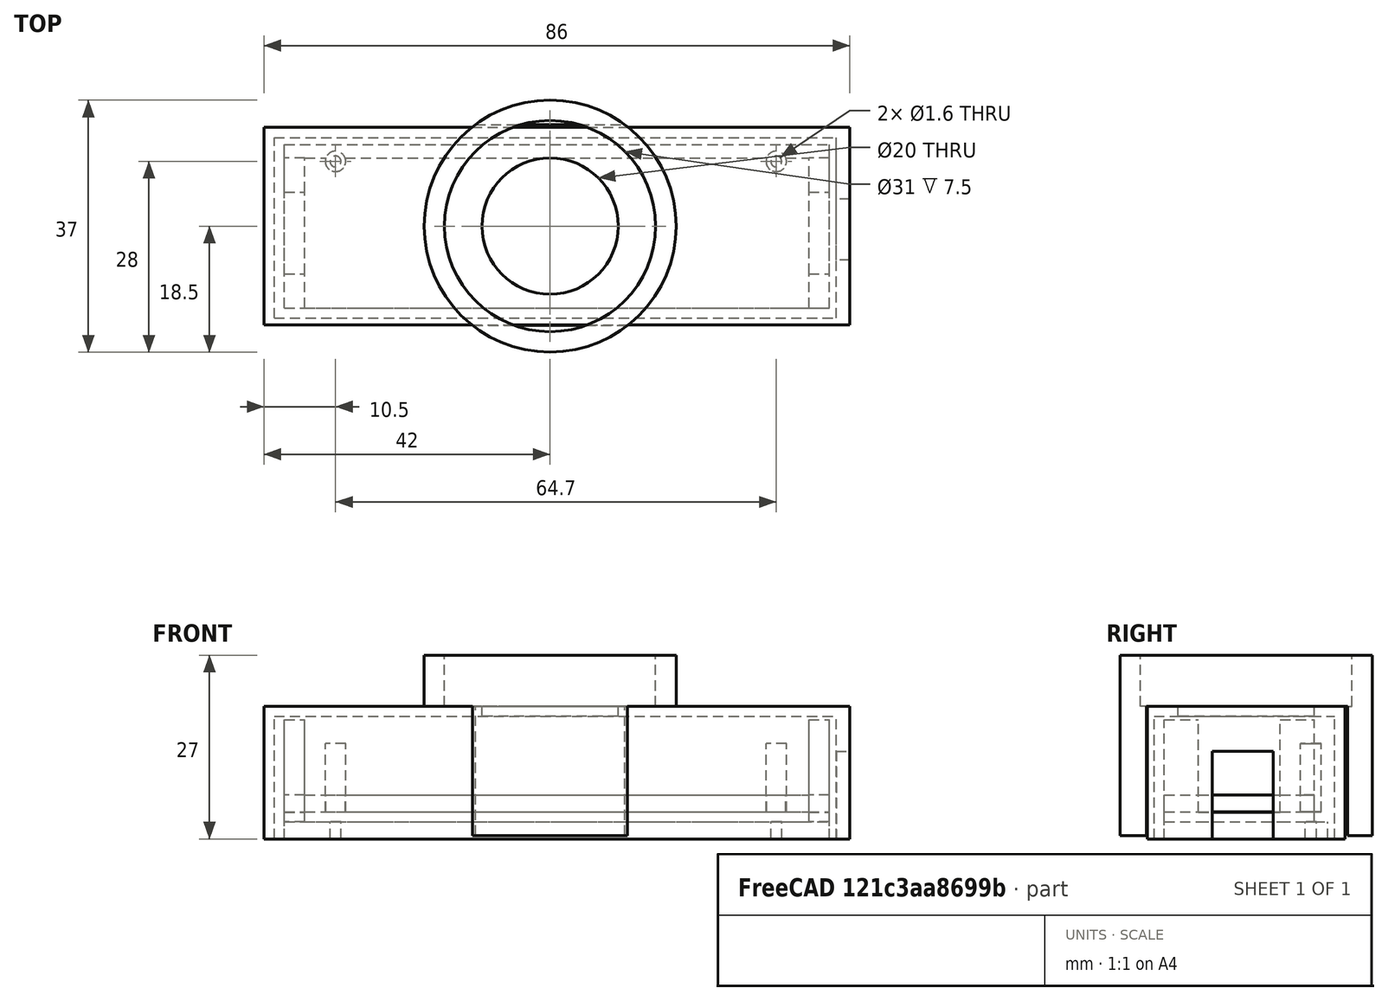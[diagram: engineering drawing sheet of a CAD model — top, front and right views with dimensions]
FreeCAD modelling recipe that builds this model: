
FCSTD DOCUMENT  (FreeCAD 0.18.4R)
Label: c920-telescope-adapter
License: All rights reserved
LicenseURL: http://en.wikipedia.org/wiki/All_rights_reserved
objects: Part::Box×19, Part::Cylinder×11, Part::MultiFuse×7, Part::Cut×7, Drawing::FeatureViewPart×1, Drawing::FeaturePage×1
note: 44 computed .brp shape members not serialized (recipe doc carries the construction recipe); baked Part::Feature solids carry a one-line shape summary decoded from their .brp

FEATURE [Part::Box] Box  label="pre-pci-board"
  AttacherType = Attacher::AttachEngine3D
  Height = 2.5
  Length = 80
  Width = 22
FEATURE [Part::Box] Box001  label="Cube"
  AttacherType = Attacher::AttachEngine3D
  Height = 10
  Length = 3
  Width = 5
FEATURE [Part::Box] Box002  label="Cube001"
  AttacherType = Attacher::AttachEngine3D
  Height = 10
  Length = 3
  Placement = pos=(77,0,0) rot=(0,0,1;0rad)
  Width = 5
FEATURE [Part::Box] Box003  label="Cube002"
  AttacherType = Attacher::AttachEngine3D
  Height = 10
  Length = 3
  Placement = pos=(77,17,0) rot=(0,0,1;0rad)
  Width = 5
FEATURE [Part::Box] Box004  label="Cube003"
  AttacherType = Attacher::AttachEngine3D
  Height = 10
  Length = 3
  Placement = pos=(0,17,0) rot=(0,0,1;0rad)
  Width = 5
FEATURE [Part::Cylinder] Cylinder
  Angle = 360
  AttacherType = Attacher::AttachEngine3D
  Height = 10
  Placement = pos=(7.5,21.5,0) rot=(0,0,1;0rad)
  Radius = 1.5
FEATURE [Part::Cylinder] Cylinder001
  Angle = 360
  AttacherType = Attacher::AttachEngine3D
  Height = 10
  Placement = pos=(72.2,21.5,0) rot=(0,0,1;0rad)
  Radius = 1.5
FEATURE [Part::MultiFuse] Fusion
  Shapes = -> [Cylinder001,Cylinder,Box004,Box003,Box002,Box001]
FEATURE [Part::Cut] Cut  label="simple-pci-board"
  Base = -> Box
  Tool = -> Fusion
FEATURE [Drawing::FeatureViewPart] Ortho  label="Ortho_0_0"
  Direction = (0,0,1)
  HiddenWidth = 0.15
  LineWidth = 0.35
  Rotation = 0
  ShowHiddenLines = false
  ShowSmoothLines = false
  Source = -> Cut
  Tolerance = 0.05
  ViewResult = <g id="Ortho_0_0"\n   transform="rotate(0,108.5,92.5) translate(108.5,92.5) scale(1,1)"\n  >\n<g   fill="none"\n   stroke="rgb(0, 0, 0)"\n   stroke-linecap="butt"\n   stroke-linejoin="miter"\n   stroke-width="0.350000"\n   transform="scale(1,-1)"\n  >\n<path id= "1" d=" M 0 5 L 0 17 " />\n<path id= "2" d=" M 3 5 L 0 5 " />\n<path id= "3" d=" M 3 17 L 0 17 " />\n<path id= "4" d=" M 3 17 L 3 22 " />\n<path id= "5" d=" M 3 22 L 6.08579 22 " />\n<path d="M6.08579 22 A1.5 1.5 0 1 1 9 21.5" /><path d="M9 21.5 A1.5 1.5 0 0 1 8.91421 22" /><path id= "8" d=" M 8.91421 22 L 70.7858 22 " />\n<path d="M70.7858 22 A1.5 1.5 0 1 1 73.7 21.5" /><path d="M73.7 21.5 A1.5 1.5 0 0 1 73.6142 22" /><path id= "11" d=" M 73.6142 22 L 77 22 " />\n<path id= "12" d=" M 77 17 L 77 22 " />\n<path id= "13" d=" M 80 17 L 77 17 " />\n<path id= "14" d=" M 80 5 L 80 17 " />\n<path id= "15" d=" M 80 5 L 77 5 " />\n<path id= "16" d=" M 77 0 L 77 5 " />\n<path id= "17" d=" M 3 0 L 77 0 " />\n<path id= "18" d=" M 3 0 L 3 5 " />\n</g>\n</g>
  Visible = true
  X = 108.5
  Y = 92.5
FEATURE [Drawing::FeaturePage] Page
  EditableTexts = Jose Damico | 2020-May-18 | 1x1 | -- | Basic Pci Board | Simple View | 1 | 1
  Group = -> [Ortho]
  Template = <path>
FEATURE [Part::Cylinder] Cylinder002
  Angle = 360
  AttacherType = Attacher::AttachEngine3D
  Height = 10
  Placement = pos=(72.2,21.5,0) rot=(0,0,1;0rad)
  Radius = 1.5
FEATURE [Part::Cylinder] Cylinder003
  Angle = 360
  AttacherType = Attacher::AttachEngine3D
  Height = 10
  Placement = pos=(7.5,21.5,0) rot=(0,0,1;0rad)
  Radius = 1.5
FEATURE [Part::Box] Box005  label="Cube004"
  AttacherType = Attacher::AttachEngine3D
  Height = 15.5
  Length = 3
  Placement = pos=(0,17,-2) rot=(0,0,1;0rad)
  Width = 5
FEATURE [Part::Box] Box006  label="Cube005"
  AttacherType = Attacher::AttachEngine3D
  Height = 15.5
  Length = 3
  Placement = pos=(77,17,-2) rot=(0,0,1;0rad)
  Width = 5
FEATURE [Part::Box] Box007  label="Cube006"
  AttacherType = Attacher::AttachEngine3D
  Height = 15.5
  Length = 3
  Placement = pos=(77,0,-2) rot=(0,0,1;0rad)
  Width = 5
FEATURE [Part::Box] Box008  label="Cube007"
  AttacherType = Attacher::AttachEngine3D
  Height = 15.5
  Length = 3
  Placement = pos=(0,0,-2) rot=(0,0,1;0rad)
  Width = 5
FEATURE [Part::Box] Box009  label="pre-pci-board001"
  AttacherType = Attacher::AttachEngine3D
  Height = 2.5
  Length = 80
  Placement = pos=(0,0,-4) rot=(0,0,1;0rad)
  Width = 24
FEATURE [Part::Box] Box010  label="Cube008"
  AttacherType = Attacher::AttachEngine3D
  Height = 2
  Length = 3
  Placement = pos=(0,5,-2.1) rot=(0,0,1;0rad)
  Width = 12
FEATURE [Part::Box] Box011  label="Cube009"
  AttacherType = Attacher::AttachEngine3D
  Height = 2
  Length = 3
  Placement = pos=(77,5,-2.1) rot=(0,0,1;0rad)
  Width = 12
FEATURE [Part::Box] Box012  label="pre-pci-board002"
  AttacherType = Attacher::AttachEngine3D
  Height = 19.5
  Length = 86
  Placement = pos=(-3,-2.5,-4) rot=(0,0,1;0rad)
  Width = 29
FEATURE [Part::MultiFuse] Fusion001
  Shapes = -> [Box011,Box010,Box008,Box007,Box006,Box005]
FEATURE [Part::Box] Box013  label="pre-pci-board003"
  AttacherType = Attacher::AttachEngine3D
  Height = 18
  Length = 82.5
  Placement = pos=(-1.5,-1.5,-4) rot=(0,0,1;0rad)
  Width = 26.5
FEATURE [Part::Cylinder] Cylinder004
  Angle = 360
  AttacherType = Attacher::AttachEngine3D
  Height = 24
  Placement = pos=(39,12,9) rot=(0,0,1;0rad)
  Radius = 10
FEATURE [Part::Box] Box014  label="cable-hole"
  AttacherType = Attacher::AttachEngine3D
  Height = 13
  Length = 8
  Placement = pos=(77,7,-4.1) rot=(0,0,1;0rad)
  Width = 9
FEATURE [Part::MultiFuse] Fusion002
  Shapes = -> [Box014,Cylinder004,Box013]
FEATURE [Part::Cut] Cut001
  Base = -> Box012
  Tool = -> Fusion002
FEATURE [Part::Cylinder] Cylinder005
  Angle = 360
  AttacherType = Attacher::AttachEngine3D
  Height = 7.5
  Placement = pos=(39,12,15.5) rot=(0,0,1;0rad)
  Radius = 15.5
FEATURE [Part::Cylinder] Cylinder006
  Angle = 360
  AttacherType = Attacher::AttachEngine3D
  Height = 26.5
  Placement = pos=(39,12,-3.5) rot=(0,0,1;0rad)
  Radius = 18.5
FEATURE [Part::Cut] Cut002
  Base = -> Cylinder006
  Tool = -> Cylinder005
FEATURE [Part::Cylinder] Cylinder007
  Angle = 360
  AttacherType = Attacher::AttachEngine3D
  Height = 24
  Placement = pos=(39,12,9) rot=(0,0,1;0rad)
  Radius = 10
FEATURE [Part::Box] Box015  label="pre-pci-board004"
  AttacherType = Attacher::AttachEngine3D
  Height = 19.5
  Length = 86
  Placement = pos=(-3,-2.5,-4) rot=(0,0,1;0rad)
  Width = 29
FEATURE [Part::Box] Box016  label="pre-pci-board005"
  AttacherType = Attacher::AttachEngine3D
  Height = 18
  Length = 82.5
  Placement = pos=(-1.5,-1.5,-4) rot=(0,0,1;0rad)
  Width = 26.5
FEATURE [Part::Box] Box017  label="cable-hole001"
  AttacherType = Attacher::AttachEngine3D
  Height = 13
  Length = 8
  Placement = pos=(77,7,-4.1) rot=(0,0,1;0rad)
  Width = 9
FEATURE [Part::MultiFuse] Fusion003
  Shapes = -> [Box017,Cylinder007,Box016]
FEATURE [Part::Cut] Cut003
  Base = -> Box015
  Tool = -> Fusion003
FEATURE [Part::Cut] Cut004
  Base = -> Cut002
  Tool = -> Cut001
FEATURE [Part::Box] Box018  label="pre-pci-board006"
  AttacherType = Attacher::AttachEngine3D
  Height = 19.5
  Length = 86
  Placement = pos=(-3,-2.6,-4) rot=(0,0,1;0rad)
  Width = 29.5
FEATURE [Part::Cylinder] Cylinder008
  Angle = 360
  AttacherType = Attacher::AttachEngine3D
  Height = 24
  Placement = pos=(39,12,9) rot=(0,0,1;0rad)
  Radius = 10
FEATURE [Part::MultiFuse] Fusion004
  Shapes = -> [Cylinder008,Box018]
FEATURE [Part::Cut] Cut005
  Base = -> Cut004
  Tool = -> Fusion004
FEATURE [Part::MultiFuse] Fusion005
  Shapes = -> [Box009,Fusion001]
FEATURE [Part::Cylinder] Cylinder009
  Angle = 360
  AttacherType = Attacher::AttachEngine3D
  Height = 10
  Placement = pos=(72.2,21.5,0) rot=(0,0,1;0rad)
  Radius = 0.8
FEATURE [Part::Cylinder] Cylinder010
  Angle = 360
  AttacherType = Attacher::AttachEngine3D
  Height = 10
  Placement = pos=(7.5,21.5,0) rot=(0,0,1;0rad)
  Radius = 0.8
FEATURE [Part::MultiFuse] Fusion006
  Placement = pos=(0,0,-6) rot=(0,0,1;0rad)
  Shapes = -> [Cylinder010,Cylinder009]
FEATURE [Part::Cut] Cut006
  Base = -> Fusion005
  Tool = -> Fusion006
note: 1 file-system path scrubbed to <path> (originals preserved in the JSON sidecar)
